# Revit family: 51372283
name_source: partatom
category: Plumbing Fixtures
revit_build: Autodesk Revit 2018 (Build: 20170223_1515(x64)
units: mm (PartAtom-declared; Revit-internal decimal feet)

## family parameters
Always vertical = Yes
Cut with Voids When Loaded = No
OmniClass Number = 23.45.55.00
OmniClass Title = Sanitary Faucets, Wastes
Part Type = Normal
Room Calculation Point = No
Round Connector Dimension = Use Diameter
Shared = No
Work Plane-Based = No

## types (1)
- 51372283 Kitchen faucet with dishwasher valve, 3 V
    2D/3D/BIM Files URL = http://static.hansa.com
    3D View = https://static.hansa.com
    Additional Features = Soft- and Needle-Spray
    Ambience photo = http://static.hansa.com
    AssetType = Fixed
    BIMObjectName = 51372283
    Backflow Prevention EN1717 = EB
    Battery = AA 1.5 V Lithium x 2
    BodyMaterial = Brass
    Brand = HANSA
    Catalog Drawing URL = http://static.hansa.com
    Category = Kitchen
    CloseOffRating = 0
    Color = Chrome
    Connection = Flexible inlet pipes
    Connection Size = G3/8
    Dimension Drawing URL = http://static.hansa.com
    Dishwasher Valve = Electronic stop valve for external equipment
    Dishwasher Valve Open Period = 4 h / 12 h
    DurationUnit = Year
    EAN Number = 4057304007101
    EMC Directive = 2014/30/EU , 2011/65/EU
    EN Standard = EN 817, EN 15091
    ETIM Class Number = EC011431 Kitchen mixing tap
    Electronic Parts = Solenoid valve;External control unit;Light indicated function(s);Low battery indicator
    FDV Document URL = http://www.hansa.com
    FaucetMainMaterial = Brass
    Features = Single-lever, side operated;Battery-operated;Dishwasher valve
    Finish = Polished
    Flow Drawing URL = http://static.hansa.com
    Flow Rate At 300kPa = 0.2 L/s
    FlowCoefficient = 0
    Group = Kitchen faucet
    IfcExportAs = IfcValveType
    IfcExportType = FAUCET
    InletConnectionSize = 10 mm  [stored 0.0328084 ft]
    Installation Type = Deck mounted
    Installation and Maintenance Guide URL = http://static.hansa.com
    Interactive AR View URL = https://static.hansa.com
    Lever Handle = Hot/Cold symbols;Single operating lever/handle
    Manufacturer = HANSA
    ManufacturerName = HANSA
    ManufacturerURL = http://www.hansa.com
    Market = International;Germany;Austria;Belgium;Netherlands;France;Czech Republic;Slovakia;Spain
    Material = Brass
    Max. Hot Water Supply = 70 °C
    Mechanical Parts = ø 40 mm ceramic cartridge for flow and temperature control;Litter filter(s)
    Mobile Product Information URL = http://mpi.hansa.com
    Model = 51372283 Kitchen faucet with dishwasher valve, 3 V
    ModelReference = 51372283
    Mounting Holes = 1 hole
    NBSDescription = Water supply fittings for wash basins and troughs
    NBSReference = 45-35-70/371
    Name = 51372283 Kitchen faucet with dishwasher valve, 3 V
    Name_en = 51372283 Kitchen faucet with dishwasher valve, 3 V
    Noise Class = I (ISO 3822)
    NominalDepth = 274 mm
    NominalHeight = 440 mm  [stored 1.44357 ft]
    NominalWidth = 123 mm
    Operating Voltage = 3 V
    Pressure Loss With Flow 02ls = 300000.0 Pa
    Product Code = 51372283
    Product Family = HANSADESIGNO Style Comfort+
    Product Image URL = http://static.hansa.com
    Product URL = http://static.hansa.com
    Protection Class = IP 55
    Revision = 4
    Sales Package dimensions (LxWxH) = 628 x 294 x 84
    Shape = Sculptured
    Short Marketing = single-lever kitchen mixer, DN 15
    Shower Spray Number = 2 shower sprays
    Size = 123x274x440 mm
    Spare-Part Information URL = http://static.hansa.com
    Spout Projection = 231 mm
    Spout Swivel Range = 150° (60° / 0°)
    Spout Type = Swivel spout;Pull-out model;Swivel range limiting option
    Surface treatment = Chrome
    Technical DataSheet URL = http://www.hansa.com
    Temperature Adjustments = Limitation option for maximum temperature and flow-rate
    UNSPSC Class Number = 30181700 Faucets or taps
    URL Declaration of Conformity = http://static.hansa.com
    URL REACH = http://static.hansa.com
    URL UN38.3 = http://www.hansa.com
    URL WEEE = http://www.hansa.com
    Uniclass2 = Pr_40_30_96_96
    Uniclass2015Description = Washbasin manual water supply sets
    Uniclass2015Reference = Pr_40_20_87_96
    Version = 4
    VersionDate = 01/07/2022
    Warranty Information URL = http://warranty.hansa.com
    WarrantyDescription = http://warranty.hansa.com
    WarrantyDurationUnit = Year
    Working Pressure = 50 - 1000 kPa
    WorkingPressure = 50 - 1000 kPa

note: [stored X ft] marks values corroborated as IEEE doubles in the binary element streams (Revit-internal decimal feet)

## geometry (parser evidence)
native form markers: Sweep x4
no freeform markers — native parametric forms only
